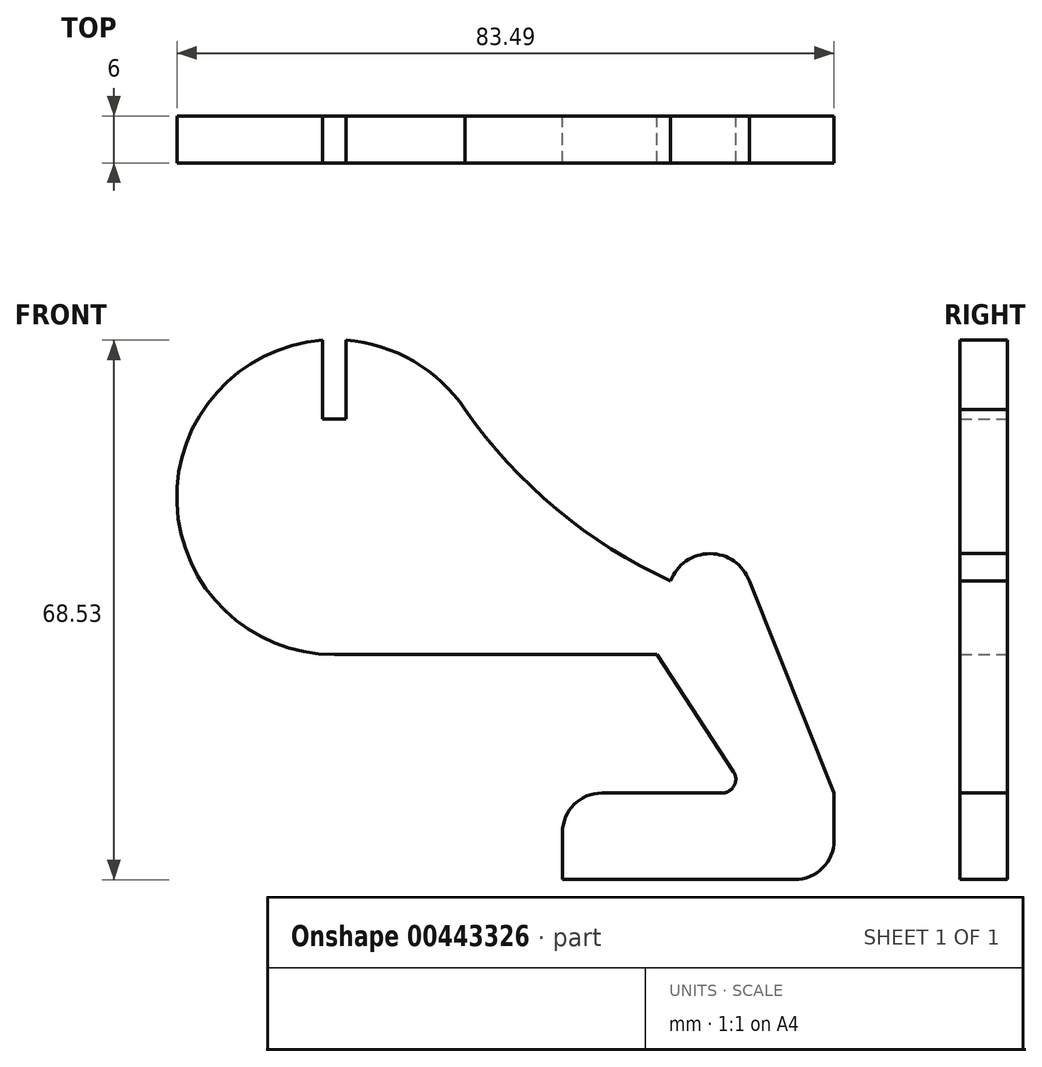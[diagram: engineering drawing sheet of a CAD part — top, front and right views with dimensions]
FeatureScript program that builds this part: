
annotation { "Feature Type Name" : "Feature", "Feature Type Description" : "" }
export const myFeature = defineFeature(function(context is Context, id is Id, definition is map)
    precondition{}
    {
        {
            var Q0;
            Q0=qCreatedBy(makeId("Front.planeOp"),FACE);
            var sketch = newSketch(context, id + "F0", { "sketchPlane" : qUnion([Q0])});
            skArc(sketch, "E0", {"start": v(-33.56, 40.34) * mm, "mid": v(-52.05, 19.64) * mm, "end": v(-32.06, 0.4) * mm});
            skLineSegment(sketch, "E1", {"start": v(-33.56, 40.34) * mm, "end": v(-33.56, 30.34) * mm});
            skLineSegment(sketch, "E2", {"start": v(-33.56, 30.34) * mm, "end": v(-30.56, 30.34) * mm});
            skLineSegment(sketch, "E3", {"start": v(-30.56, 30.34) * mm, "end": v(-30.56, 40.34) * mm});
            skArc(sketch, "E4", {"start": v(-15.45, 31.52) * mm, "mid": v(-3.84, 18.9) * mm, "end": v(10.66, 9.74) * mm});
            skArc(sketch, "E5", {"start": v(20.66, 9.74) * mm, "mid": v(15.66, 13.23) * mm, "end": v(10.66, 9.74) * mm});
            skLineSegment(sketch, "E6", {"start": v(20.66, 9.74) * mm, "end": v(31.43, -17.19) * mm});
            skLineSegment(sketch, "E7", {"start": v(-32.06, 0.4) * mm, "end": v(8.94, 0.4) * mm});
            skLineSegment(sketch, "E8", {"start": v(8.94, 0.4) * mm, "end": v(18.66, -14.48) * mm});
            skLineSegment(sketch, "E9", {"start": v(31.43, -17.19) * mm, "end": v(31.43, -23.19) * mm});
            skLineSegment(sketch, "E10", {"start": v(17.2, -17.19) * mm, "end": v(1.93, -17.19) * mm});
            skPoint(sketch, "E11", {"position": v(0.43, -17.19) * mm});
            skLineSegment(sketch, "E12", {"start": v(26.43, -28.19) * mm, "end": v(-3.07, -28.19) * mm});
            skLineSegment(sketch, "E13", {"start": v(-3.07, -22.19) * mm, "end": v(-3.07, -28.19) * mm});
            skPoint(sketch, "E14.visualSharp", {"position": v(31.43, -28.19) * mm});
            skArc(sketch, "E14.filletArc", {"start": v(26.43, -28.19) * mm, "mid": v(29.96, -26.72) * mm, "end": v(31.43, -23.19) * mm});
            skPoint(sketch, "E15.visualSharp", {"position": v(-3.07, -17.19) * mm});
            skArc(sketch, "E15.filletArc", {"start": v(1.93, -17.19) * mm, "mid": v(-1.6, -18.65) * mm, "end": v(-3.07, -22.19) * mm});
            skArc(sketch, "E16.trimOffspring", {"start": v(-15.45, 31.52) * mm, "mid": v(-22, 37.67) * mm, "end": v(-30.56, 40.34) * mm});
            skPoint(sketch, "E17.visualSharp", {"position": v(20.43, -17.19) * mm});
            skArc(sketch, "E17.filletArc", {"start": v(17.2, -17.19) * mm, "mid": v(18.73, -16.27) * mm, "end": v(18.66, -14.48) * mm});
            skSolve(sketch);
        }
        {
            var Q0;
            Q0=makeQuery(id+"F0.imprint","IMPRINT",FACE,{"disambiguationData":[TD([[makeQuery(id+"F0.imprint","IMPRINT",EDGE,{"derivedFrom":sQuery(id+"F0.wireOp",EDGE,"E0")}),1.0]])]});
            extrude(context, id + "F1", {"entities" : qUnion([Q0]), "depth" : 3 * mm, "hasSecondDirection" : true, "secondDirectionOppositeDirection" : true, "secondDirectionDepth" : 3 * mm});
        }
    });
